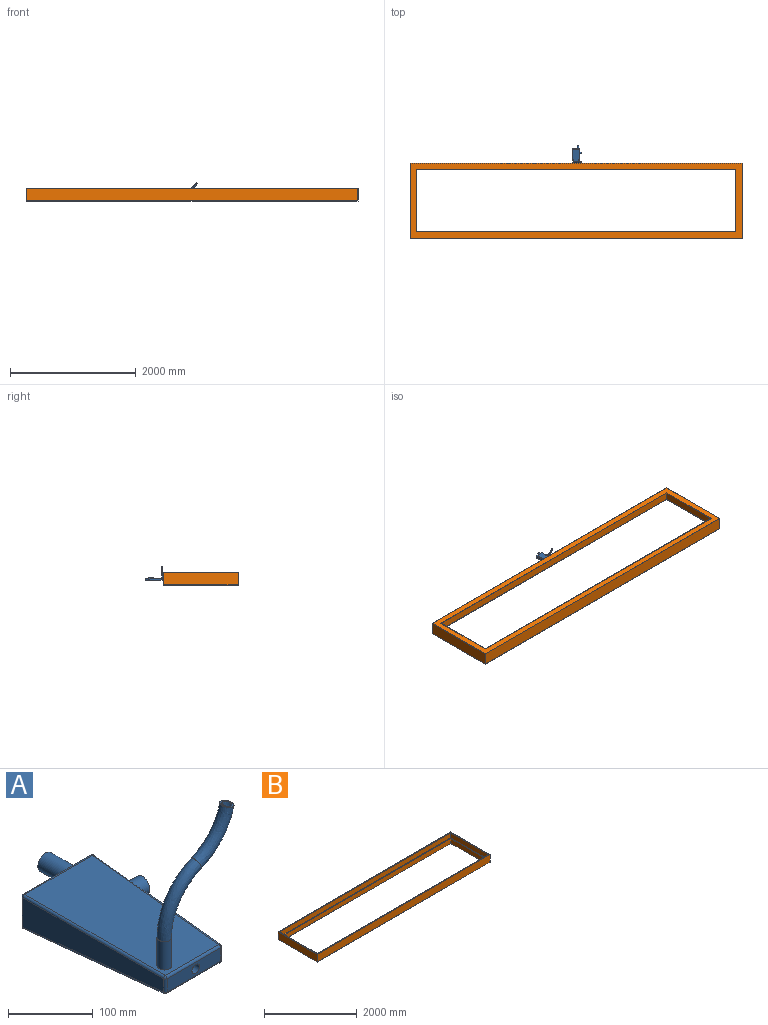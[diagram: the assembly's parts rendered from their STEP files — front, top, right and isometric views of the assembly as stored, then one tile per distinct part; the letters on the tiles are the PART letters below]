
ASSEMBLY  parts=2 mates=1
PART A: 62 faces, bbox 144.2x281.8x223.4 mm
  f0: plane 224.63x114.9mm, normal (0,-0.05,1), area 22219.3mm2, adj f1,f28,f29,f30,f31
  f1: cylinder r=3.17mm len=112.52mm, axis (-1,0,0), area 579.9mm2, adj f0,f2,f24,f27
  f2: sphere r=3.17mm, area 16.9mm2, adj f1,f3,f30
  f3: cylinder r=3.17mm len=42.67mm, axis (0,0,-1), area 219.9mm2, adj f2,f4,f23,f24
  f4: plane 222.25x42.67mm, normal (-1,-0.05,0), area 6904mm2, adj f3,f5,f22,f30
  f5: cylinder r=3.17mm len=19.37mm, axis (0,0,1), area 93.4mm2, adj f4,f6,f7,f21
  f6: sphere r=3.17mm, area 9.6mm2, adj f5,f29,f30
  f7: plane 89.22x19.37mm, normal (0,-1,0), area 1602mm2, adj f5,f8,f9,f20,f29
  f8: cylinder r=6.35mm len=228.6mm, axis (0,-1,0), area 9120.7mm2, adj f7,f24
  f9: cylinder r=3.17mm len=19.37mm, axis (0,0,1), area 93.4mm2, adj f7,f10,f11,f19
  f10: sphere r=3.17mm, area 9.6mm2, adj f9,f28,f29
  f11: plane 222.25x42.67mm, normal (1,-0.05,0), area 6443.3mm2, adj f9,f12,f16,f17,f28
  f12: cylinder r=3.17mm len=42.67mm, axis (0,0,-1), area 219.9mm2, adj f11,f13,f24,f27
  f13: sphere r=3.17mm, area 16.9mm2, adj f12,f14,f16
  f14: cylinder r=3.17mm len=112.52mm, axis (-1,0,0), area 579.9mm2, adj f13,f15,f23,f24
  f15: plane 222.25x112.52mm, normal (0,-0.05,-1), area 22449.5mm2, adj f14,f16,f20,f22
  f16: cylinder r=3.17mm len=222.32mm, axis (-0.05,-1,0.05), area 1109.5mm2, adj f11,f13,f15,f19
  f17: cylinder r=12.11mm len=26.63mm, axis (-1,0.05,0), area 1932.8mm2, adj f11,f18
  f18: plane 24.22x24.19mm, normal (1,-0.05,0), area 460.8mm2, adj f17
  f19: sphere r=3.17mm, area 9.6mm2, adj f9,f16,f20
  f20: cylinder r=3.17mm len=89.22mm, axis (1,0,0), area 430.2mm2, adj f7,f15,f19,f21
  f21: sphere r=3.17mm, area 9.6mm2, adj f5,f20,f22
  f22: cylinder r=3.17mm len=222.32mm, axis (0.05,-1,0.05), area 1109.5mm2, adj f4,f15,f21,f23
  f23: sphere r=3.17mm, area 16.9mm2, adj f3,f14,f22
  f24: plane 112.52x42.67mm, normal (0,1,0), area 4167.7mm2, adj f1,f3,f8,f12,f14,f25
  f25: cylinder r=12.7mm len=50.8mm, axis (0,-1,0), area 4053.7mm2, adj f24,f26
  f26: plane 25.4x25.4mm, normal (0,1,0), area 506.7mm2, adj f25
  f27: sphere r=3.17mm, area 16.9mm2, adj f1,f12,f28
  f28: cylinder r=3.17mm len=222.32mm, axis (-0.05,-1,-0.05), area 1109.5mm2, adj f0,f10,f11,f27
  f29: cylinder r=3.17mm len=89.22mm, axis (1,0,0), area 430.2mm2, adj f0,f6,f7,f10
  f30: cylinder r=3.17mm len=222.32mm, axis (0.05,-1,-0.05), area 1109.5mm2, adj f0,f2,f4,f6
  f31: bspline ~42.53x34.19mm, area 2193.8mm2, adj f0,f32
  f32: bspline ~89.32x66.56mm, area 5504.4mm2, adj f31,f33
  f33: bspline ~69.93x62.5mm, area 4399.5mm2, adj f32,f34
  f34: plane 19.48x19.06mm, normal (0.23,-0.05,0.97), area 116.4mm2, adj f33
  f35: plane 222.25x112.52mm, normal (0,0.05,-1), area 22335.8mm2, adj f36,f59,f60,f61
  f36: cylinder r=0.64mm len=89.22mm, axis (1,0,0), area 86mm2, adj f35,f37,f57,f58
  f37: sphere r=0.64mm, area 0.4mm2, adj f36,f38,f59
  f38: cylinder r=0.64mm len=19.37mm, axis (0,0,1), area 18.7mm2, adj f37,f39,f56,f57
  f39: sphere r=0.64mm, area 0.4mm2, adj f38,f40,f55
  f40: cylinder r=0.64mm len=222.26mm, axis (-0.05,-1,0.05), area 221.9mm2, adj f39,f41,f54,f56
  f41: sphere r=0.64mm, area 0.7mm2, adj f40,f42,f53
  f42: cylinder r=0.64mm len=42.67mm, axis (0,0,-1), area 44mm2, adj f41,f43,f44,f56
  f43: sphere r=0.64mm, area 0.7mm2, adj f42,f59,f60
  f44: plane 112.52x42.67mm, normal (0,-1,0), area 4552.8mm2, adj f42,f45,f46,f53,f60
  f45: cylinder r=8.89mm len=223.52mm, axis (0,-1,0), area 12485.3mm2, adj f44,f57
  f46: cylinder r=0.64mm len=42.67mm, axis (0,0,-1), area 44mm2, adj f44,f47,f51,f52
  f47: sphere r=0.64mm, area 0.7mm2, adj f46,f48,f53
  f48: cylinder r=0.64mm len=222.26mm, axis (0.05,-1,0.05), area 221.9mm2, adj f47,f49,f52,f54
  f49: sphere r=0.64mm, area 0.4mm2, adj f48,f50,f55
  f50: cylinder r=0.64mm len=19.37mm, axis (0,0,1), area 18.7mm2, adj f49,f52,f57,f58
  f51: sphere r=0.64mm, area 0.7mm2, adj f46,f60,f61
  f52: plane 222.25x42.67mm, normal (1,0.05,0), area 6904mm2, adj f46,f48,f50,f61
  f53: cylinder r=0.64mm len=112.52mm, axis (-1,0,0), area 116mm2, adj f41,f44,f47,f54
  f54: plane 222.25x112.52mm, normal (0,0.05,1), area 22449.5mm2, adj f40,f48,f53,f55
  f55: cylinder r=0.64mm len=89.22mm, axis (1,0,0), area 86mm2, adj f39,f49,f54,f57
  f56: plane 222.25x42.67mm, normal (-1,0.05,0), area 6904mm2, adj f38,f40,f42,f59
  f57: plane 89.22x19.37mm, normal (0,1,0), area 1480.3mm2, adj f36,f38,f45,f50,f55
  f58: sphere r=0.64mm, area 0.4mm2, adj f36,f50,f61
  f59: cylinder r=0.64mm len=222.26mm, axis (-0.05,-1,-0.05), area 221.9mm2, adj f35,f37,f43,f56
  f60: cylinder r=0.64mm len=112.52mm, axis (-1,0,0), area 116mm2, adj f35,f43,f44,f51
  f61: cylinder r=0.64mm len=222.26mm, axis (0.05,-1,-0.05), area 221.9mm2, adj f35,f51,f52,f58
PART B: 30 faces, bbox 5283.2x1193.8x203.2 mm
  f0: plane 1187.45x196.85mm, normal (1,0,0), area 233749.5mm2, adj f1,f7,f17,f24
  f1: plane 5276.85x196.85mm, normal (0,-1,0), area 1038747.9mm2, adj f0,f2,f17,f24
  f2: plane 1187.45x196.85mm, normal (-1,0,0), area 233749.5mm2, adj f1,f7,f17,f24
  f3: plane 5283.2x203.2mm, normal (0,1,0), area 1073546.2mm2, adj f4,f6,f8,f29
  f4: plane 1193.8x203.2mm, normal (-1,0,0), area 242580.2mm2, adj f3,f5,f8,f29
  f5: plane 5283.2x203.2mm, normal (0,-1,0), area 1073546.2mm2, adj f4,f6,f8,f29
  f6: plane 1193.8x203.2mm, normal (1,0,0), area 242580.2mm2, adj f3,f5,f8,f29
  f7: plane 5276.85x196.85mm, normal (0,1,0), area 1038747.9mm2, adj f0,f2,f17,f24
  f8: plane 5283.2x1193.8mm, normal (0,0,-1), area 1274836.2mm2, adj f3,f4,f5,f6,f9,f10,f11,f16
  f9: plane 990.6x127mm, normal (1,0,0), area 125806.2mm2, adj f8,f10,f16,f22
  f10: plane 5080x127mm, normal (0,-1,0), area 645160mm2, adj f8,f9,f11,f22
  f11: plane 990.6x127mm, normal (-1,0,0), area 125806.2mm2, adj f8,f10,f16,f22
  f12: plane 5086.35x120.65mm, normal (0,1,0), area 613668.1mm2, adj f13,f15,f17,f23
  f13: plane 996.95x120.65mm, normal (-1,0,0), area 120282mm2, adj f12,f14,f17,f23
  f14: plane 5086.35x120.65mm, normal (0,-1,0), area 613668.1mm2, adj f13,f15,f17,f23
  f15: plane 996.95x120.65mm, normal (1,0,0), area 120282mm2, adj f12,f14,f17,f23
  f16: plane 5080x127mm, normal (0,1,0), area 645160mm2, adj f8,f9,f11,f22
  f17: plane 5276.85x1187.45mm, normal (0,0,1), area 1195158.9mm2, adj f0,f1,f2,f7,f12,f13,f14,f15
  f18: plane 1041.4x3.18mm, normal (1,0,0), area 3306.4mm2, adj f19,f21,f22,f23
  f19: plane 5130.8x3.18mm, normal (0,1,0), area 16290.3mm2, adj f18,f20,f22,f23
  f20: plane 1041.4x3.18mm, normal (-1,0,0), area 3306.4mm2, adj f19,f21,f22,f23
  f21: plane 5130.8x3.18mm, normal (0,-1,0), area 16290.3mm2, adj f18,f20,f22,f23
  f22: plane 5130.8x1041.4mm, normal (0,0,1), area 310967.1mm2, adj f9,f10,f11,f16,f18,f19,f20,f21
  f23: plane 5130.8x1041.4mm, normal (0,0,-1), area 272378.5mm2, adj f12,f13,f14,f15,f18,f19,f20,f21
  f24: plane 5276.85x1187.45mm, normal (0,0,-1), area 285362.3mm2, adj f0,f1,f2,f7,f25,f26,f27,f28
  f25: plane 1143x3.18mm, normal (-1,0,0), area 3629mm2, adj f24,f26,f28,f29
  f26: plane 5232.4x3.18mm, normal (0,1,0), area 16612.9mm2, adj f24,f25,f27,f29
  f27: plane 1143x3.18mm, normal (1,0,0), area 3629mm2, adj f24,f26,f28,f29
  f28: plane 5232.4x3.18mm, normal (0,-1,0), area 16612.9mm2, adj f24,f25,f27,f29
  f29: plane 5283.2x1193.8mm, normal (0,0,1), area 326451mm2, adj f3,f4,f5,f6,f25,f26,f27,f28
PLACE A at identity fixed
PLACE B rot(axis=(1,0,0),180deg) t=(-2593.98,0,123.99)mm
MATE fastened A.f7 <-> B.f5  axis (0,-1,0) through (47.63,0,22.39)mm
